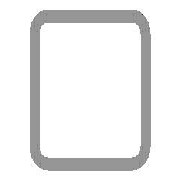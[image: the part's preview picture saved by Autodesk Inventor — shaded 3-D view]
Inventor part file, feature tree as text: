
AUTODESK INVENTOR PART (.ipt)
format: ipt  version: 2025 (Build 290162010, 162A)  size: 133,632 bytes
history: native  units: mm (DEFAULTED — no unit token found)
features: other x4, sketch x1, plane x1
ambient origin geometry x8: Origin, YZ Plane, XZ Plane, XY Plane, X Axis, Y Axis, Z Axis, Center Point
bodies: Solid1 (feature_tree), Body (feature_tree)
feature tree (6):
  parser-record x1  (decoder bookkeeping rows leaked as tree rows — omitted from the tree; the rows remain in map.json)
  other  "Driven Length"
  other  "Start Plane"
  other  "End Plane"
  sketch  "Sketch3"  dims[d3=120.0mm d4=0.0mm d7=4.0mm d9=40.0mm d11=40.0mm d12=2.0mm d13=40.0mm d14=160.0mm d15=20.0mm d16=20.0mm d17=90.0deg d18=120.0mm]
  plane  "Work Plane3"
